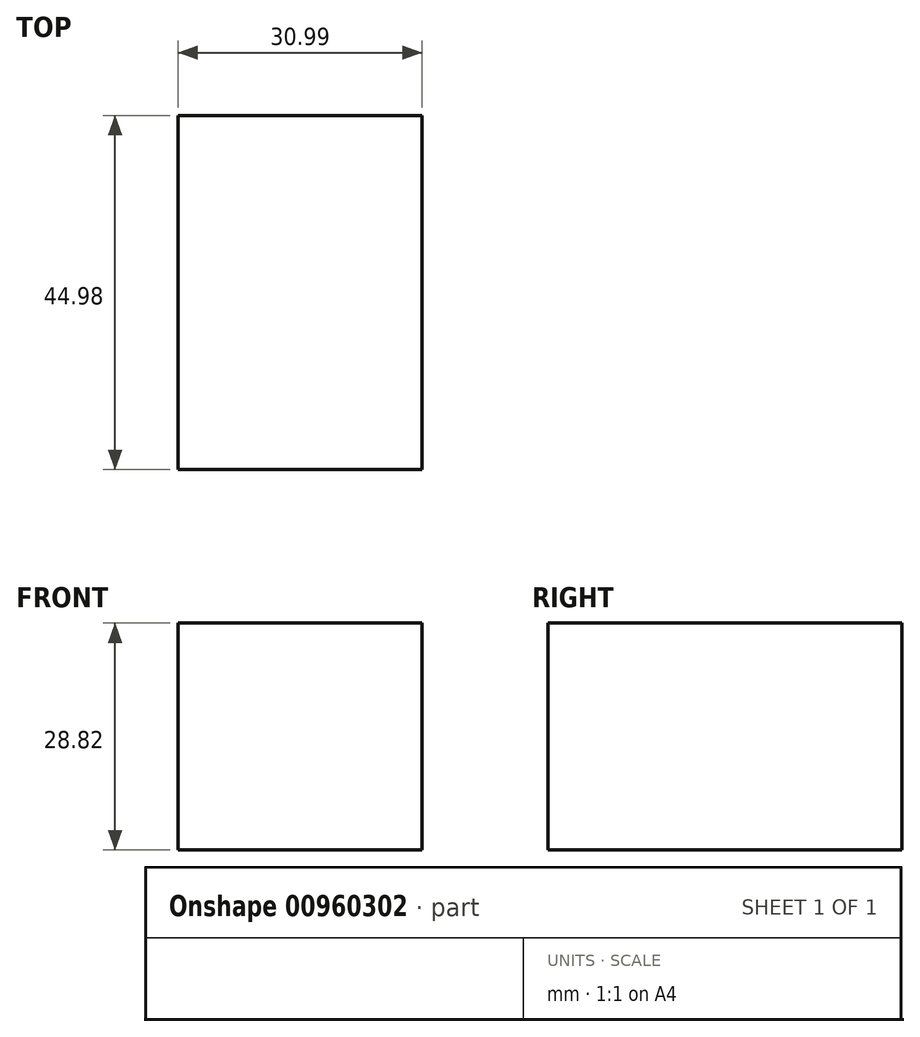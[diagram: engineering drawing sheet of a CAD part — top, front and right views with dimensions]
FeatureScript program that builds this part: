
annotation { "Feature Type Name" : "Feature", "Feature Type Description" : "" }
export const myFeature = defineFeature(function(context is Context, id is Id, definition is map)
    precondition{}
    {
        {
            var Q0;
            Q0=qCreatedBy(makeId("Right.planeOp"),FACE);
            var sketch = newSketch(context, id + "F0", { "sketchPlane" : qUnion([Q0])});
            skLineSegment(sketch, "E0.bottom", {"start": v(0, 0) * mm, "end": v(-44.98, 0) * mm});
            skLineSegment(sketch, "E0.top", {"start": v(0, 28.82) * mm, "end": v(-44.98, 28.82) * mm});
            skLineSegment(sketch, "E0.left", {"start": v(0, 0) * mm, "end": v(0, 28.82) * mm});
            skLineSegment(sketch, "E0.right", {"start": v(-44.98, 0) * mm, "end": v(-44.98, 28.82) * mm});
            skSolve(sketch);
        }
        {
            var Q0;
            Q0 = qSketchRegion(id + "F0", true);
            var Q1;
            Q1=makeQuery(id+"F0.imprint","IMPRINT",FACE,{"disambiguationData":[TD([[makeQuery(id+"F0.imprint","IMPRINT",EDGE,{"derivedFrom":sQuery(id+"F0.wireOp",EDGE,"E0.bottom")}),-1.0]])]});
            extrude(context, id + "F1", {"entities" : qUnion([Q0, Q1]), "depth" : 30.99 * mm, "offsetDistance" : 25.4 * mm});
        }
    });
